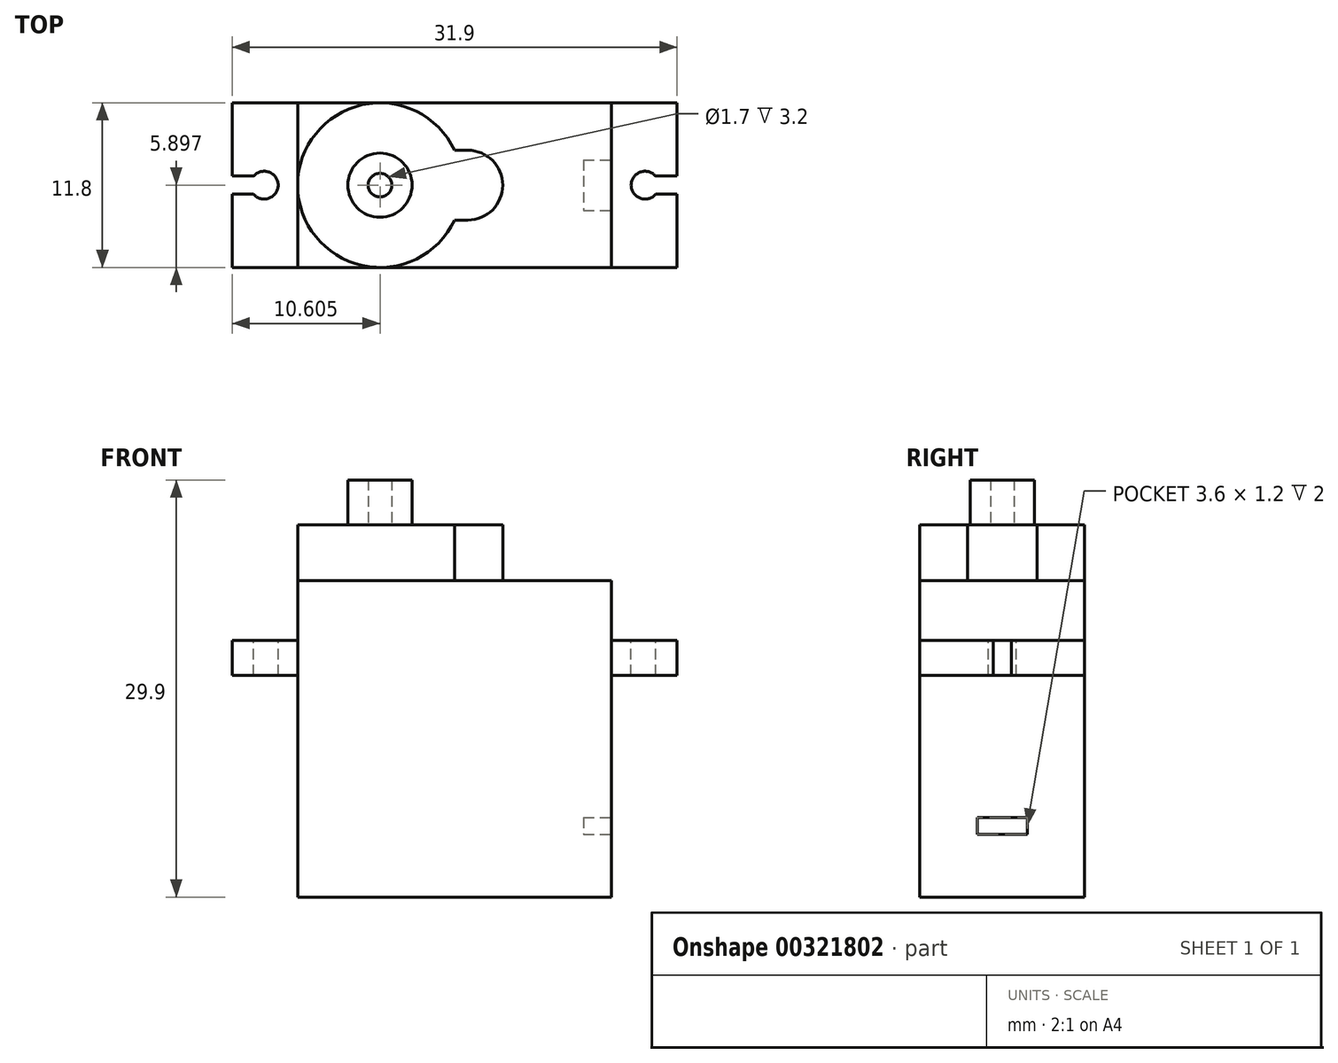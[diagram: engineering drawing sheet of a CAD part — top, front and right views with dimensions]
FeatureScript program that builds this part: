
annotation { "Feature Type Name" : "Feature", "Feature Type Description" : "" }
export const myFeature = defineFeature(function(context is Context, id is Id, definition is map)
    precondition{}
    {
        {
            var Q0;
            Q0=qCreatedBy(makeId("Top.planeOp"),FACE);
            var sketch = newSketch(context, id + "F0", { "sketchPlane" : qUnion([Q0])});
            skLineSegment(sketch, "E0.bottom", {"start": v(-53.59, 15.06) * mm, "end": v(-31.09, 15.06) * mm});
            skLineSegment(sketch, "E0.top", {"start": v(-53.59, 3.26) * mm, "end": v(-31.09, 3.26) * mm});
            skLineSegment(sketch, "E0.left", {"start": v(-53.59, 15.06) * mm, "end": v(-53.59, 3.26) * mm});
            skLineSegment(sketch, "E0.right", {"start": v(-31.09, 15.06) * mm, "end": v(-31.09, 3.26) * mm});
            skSolve(sketch);
        }
        {
            var Q0;
            Q0=makeQuery(id+"F0.imprint","IMPRINT",FACE,{"disambiguationData":[TD([[makeQuery(id+"F0.imprint","IMPRINT",EDGE,{"derivedFrom":sQuery(id+"F0.wireOp",EDGE,"E0.bottom")}),-1.0]])]});
            extrude(context, id + "F1", {"entities" : qUnion([Q0]), "depth" : 22.7 * mm});
        }
        {
            var Q0;
            Q0=makeQuery(id+"F1.opExtrude","SWEPT_FACE",FACE,{"disambiguationData":[OSD([sQuery(id+"F0.wireOp",EDGE,"E0.top")])]});
            var sketch = newSketch(context, id + "F2", { "sketchPlane" : qUnion([Q0])});
            skLineSegment(sketch, "E1.right", {"start": v(-31.09, 0) * mm, "end": v(-31.09, 15.9) * mm});
            skLineSegment(sketch, "E2.bottom", {"start": v(-53.59, 15.9) * mm, "end": v(-58.29, 15.9) * mm});
            skLineSegment(sketch, "E2.top", {"start": v(-53.59, 18.4) * mm, "end": v(-58.29, 18.4) * mm});
            skLineSegment(sketch, "E2.left", {"start": v(-53.59, 15.9) * mm, "end": v(-53.59, 18.4) * mm});
            skLineSegment(sketch, "E2.right", {"start": v(-58.29, 15.9) * mm, "end": v(-58.29, 18.4) * mm});
            skLineSegment(sketch, "E3.bottom", {"start": v(-31.09, 15.9) * mm, "end": v(-26.39, 15.9) * mm});
            skLineSegment(sketch, "E3.top", {"start": v(-31.09, 18.4) * mm, "end": v(-26.39, 18.4) * mm});
            skLineSegment(sketch, "E3.left", {"start": v(-31.09, 15.9) * mm, "end": v(-31.09, 18.4) * mm});
            skLineSegment(sketch, "E3.right", {"start": v(-26.39, 15.9) * mm, "end": v(-26.39, 18.4) * mm});
            skSolve(sketch);
        }
        {
            var Q0;
            Q0=makeQuery(id+"F2.imprint","IMPRINT",FACE,{"disambiguationData":[TD([[makeQuery(id+"F2.imprint","IMPRINT",EDGE,{"derivedFrom":sQuery(id+"F2.wireOp",EDGE,"E2.bottom")}),-1.0]])]});
            var Q1;
            Q1=makeQuery(id+"F2.imprint","IMPRINT",FACE,{"disambiguationData":[TD([[makeQuery(id+"F2.imprint","IMPRINT",EDGE,{"derivedFrom":sQuery(id+"F2.wireOp",EDGE,"E3.bottom")}),1.0]])]});
            extrude(context, id + "F3", {"entities" : qUnion([Q0, Q1]), "oppositeDirection" : true, "depth" : 11.8 * mm});
        }
        {
            var Q0;
            Q0=makeQuery(id+"F3.opExtrude","SWEPT_FACE",FACE,{"disambiguationData":[OSD([sQuery(id+"F2.wireOp",EDGE,"E2.top")])]});
            var sketch = newSketch(context, id + "F4", { "sketchPlane" : qUnion([Q0])});
            skPoint(sketch, "E4.endSnap0", {"position": v(-58.29, 9.16) * mm});
            skArc(sketch, "E5", {"start": v(-56.75, 8.5) * mm, "mid": v(-54.99, 9.16) * mm, "end": v(-56.75, 9.8) * mm});
            skLineSegment(sketch, "E6", {"start": v(-58.29, 9.16) * mm, "end": v(-58.29, 8.5) * mm});
            skLineSegment(sketch, "E7", {"start": v(-58.29, 8.5) * mm, "end": v(-56.75, 8.5) * mm});
            skLineSegment(sketch, "E8", {"start": v(-58.29, 9.16) * mm, "end": v(-58.29, 9.8) * mm});
            skLineSegment(sketch, "E9", {"start": v(-58.29, 9.8) * mm, "end": v(-56.75, 9.8) * mm});
            skSolve(sketch);
        }
        {
            var Q0;
            Q0=makeQuery(id+"F4.imprint","IMPRINT",FACE,{"disambiguationData":[TD([[makeQuery(id+"F4.imprint","IMPRINT",EDGE,{"derivedFrom":sQuery(id+"F4.wireOp",EDGE,"E5")}),1.0]])]});
            extrude(context, id + "F5", {"entities" : qUnion([Q0]), "operationType" : NewBodyOperationType.REMOVE, "oppositeDirection" : true, "depth" : 2.5 * mm});
        }
        {
            var Q0;
            Q0=makeQuery(id+"F3.opExtrude","SWEPT_FACE",FACE,{"disambiguationData":[OSD([sQuery(id+"F2.wireOp",EDGE,"E3.top")])]});
            var sketch = newSketch(context, id + "F6", { "sketchPlane" : qUnion([Q0])});
            skPoint(sketch, "E10.endSnap0", {"position": v(-26.39, 9.16) * mm});
            skArc(sketch, "E11", {"start": v(-27.93, 9.8) * mm, "mid": v(-29.69, 9.16) * mm, "end": v(-27.93, 8.5) * mm});
            skLineSegment(sketch, "E12", {"start": v(-26.39, 9.16) * mm, "end": v(-26.39, 8.5) * mm});
            skLineSegment(sketch, "E13", {"start": v(-26.39, 8.5) * mm, "end": v(-27.93, 8.5) * mm});
            skLineSegment(sketch, "E14", {"start": v(-26.39, 9.16) * mm, "end": v(-26.39, 9.8) * mm});
            skLineSegment(sketch, "E15", {"start": v(-26.39, 9.8) * mm, "end": v(-27.93, 9.8) * mm});
            skSolve(sketch);
        }
        {
            var Q0;
            Q0=makeQuery(id+"F6.imprint","IMPRINT",FACE,{"disambiguationData":[TD([[makeQuery(id+"F6.imprint","IMPRINT",EDGE,{"derivedFrom":sQuery(id+"F6.wireOp",EDGE,"E11")}),1.0]])]});
            extrude(context, id + "F7", {"entities" : qUnion([Q0]), "operationType" : NewBodyOperationType.REMOVE, "oppositeDirection" : true, "depth" : 2.5 * mm});
        }
        {
            var Q0;
            Q0=makeQuery(id+"F1.opExtrude","CAP_FACE",FACE,{"disambiguationData":[OSD([sQuery(id+"F0.wireOp",EDGE,"E0.bottom"),sQuery(id+"F0.wireOp",EDGE,"E0.top"),sQuery(id+"F0.wireOp",EDGE,"E0.left"),sQuery(id+"F0.wireOp",EDGE,"E0.right")])],"isStart":false});
            var sketch = newSketch(context, id + "F8", { "sketchPlane" : qUnion([Q0])});
            skArc(sketch, "E16", {"start": v(-42.34, 11.66) * mm, "mid": v(-53.59, 9.16) * mm, "end": v(-42.34, 6.66) * mm});
            skPoint(sketch, "E17.endSnap0", {"position": v(-31.09, 9.16) * mm});
            skArc(sketch, "E18", {"start": v(-41.39, 6.66) * mm, "mid": v(-38.89, 9.16) * mm, "end": v(-41.39, 11.66) * mm});
            skLineSegment(sketch, "E19", {"start": v(-41.39, 11.66) * mm, "end": v(-42.34, 11.66) * mm});
            skLineSegment(sketch, "E20.MirrorCS", {"start": v(-41.39, 6.66) * mm, "end": v(-42.34, 6.66) * mm});
            skPoint(sketch, "E17.start.orphan", {"position": v(-31.09, 9.16) * mm});
            skPoint(sketch, "E21.start.orphan", {"position": v(-53.59, 9.16) * mm});
            skSolve(sketch);
        }
        {
            var Q0;
            Q0=makeQuery(id+"F8.imprint","IMPRINT",FACE,{"disambiguationData":[TD([[makeQuery(id+"F8.imprint","IMPRINT",EDGE,{"derivedFrom":sQuery(id+"F8.wireOp",EDGE,"E18")}),1.0]])]});
            extrude(context, id + "F9", {"entities" : qUnion([Q0]), "operationType" : NewBodyOperationType.ADD, "depth" : 4 * mm});
        }
        {
            var Q0;
            Q0=makeQuery(id+"F9.opExtrude","CAP_FACE",FACE,{"disambiguationData":[OSD([sQuery(id+"F8.wireOp",EDGE,"E16"),sQuery(id+"F8.wireOp",EDGE,"E18"),sQuery(id+"F8.wireOp",EDGE,"E19"),sQuery(id+"F8.wireOp",EDGE,"E20.MirrorCS")])],"isStart":false});
            var sketch = newSketch(context, id + "F10", { "sketchPlane" : qUnion([Q0])});
            skPoint(sketch, "E22.endSnap0", {"position": v(-53.59, 9.16) * mm});
            skCircle(sketch, "E23", {"center": v(-47.69, 9.16) * mm, "radius": 2.3 * mm});
            skCircle(sketch, "E24", {"center": v(-47.69, 9.16) * mm, "radius": 0.85 * mm});
            skSolve(sketch);
        }
        {
            var Q0;
            Q0=makeQuery(id+"F10.imprint","IMPRINT",FACE,{"disambiguationData":[TD([[makeQuery(id+"F10.imprint","IMPRINT",EDGE,{"derivedFrom":sQuery(id+"F10.wireOp",EDGE,"E23")}),1.0]])]});
            extrude(context, id + "F11", {"entities" : qUnion([Q0]), "operationType" : NewBodyOperationType.ADD, "depth" : 3.2 * mm});
        }
        {
            var Q0;
            Q0=makeQuery(id+"F1.opExtrude","SWEPT_FACE",FACE,{"disambiguationData":[OSD([sQuery(id+"F0.wireOp",EDGE,"E0.right")])]});
            var sketch = newSketch(context, id + "F12", { "sketchPlane" : qUnion([Q0])});
            skLineSegment(sketch, "E25", {"start": v(9.16, 4.5) * mm, "end": v(7.36, 4.5) * mm});
            skLineSegment(sketch, "E26", {"start": v(7.36, 4.5) * mm, "end": v(7.36, 5.7) * mm});
            skLineSegment(sketch, "E27", {"start": v(7.36, 5.7) * mm, "end": v(10.96, 5.7) * mm});
            skLineSegment(sketch, "E28", {"start": v(10.96, 5.7) * mm, "end": v(10.96, 4.5) * mm});
            skLineSegment(sketch, "E29", {"start": v(10.96, 4.5) * mm, "end": v(9.16, 4.5) * mm});
            skSolve(sketch);
        }
        {
            var Q0;
            Q0=makeQuery(id+"F12.imprint","IMPRINT",FACE,{"disambiguationData":[TD([[makeQuery(id+"F12.imprint","IMPRINT",EDGE,{"derivedFrom":sQuery(id+"F12.wireOp",EDGE,"E25")}),-1.0]])]});
            extrude(context, id + "F13", {"entities" : qUnion([Q0]), "operationType" : NewBodyOperationType.REMOVE, "oppositeDirection" : true, "depth" : 2 * mm});
        }
    });
